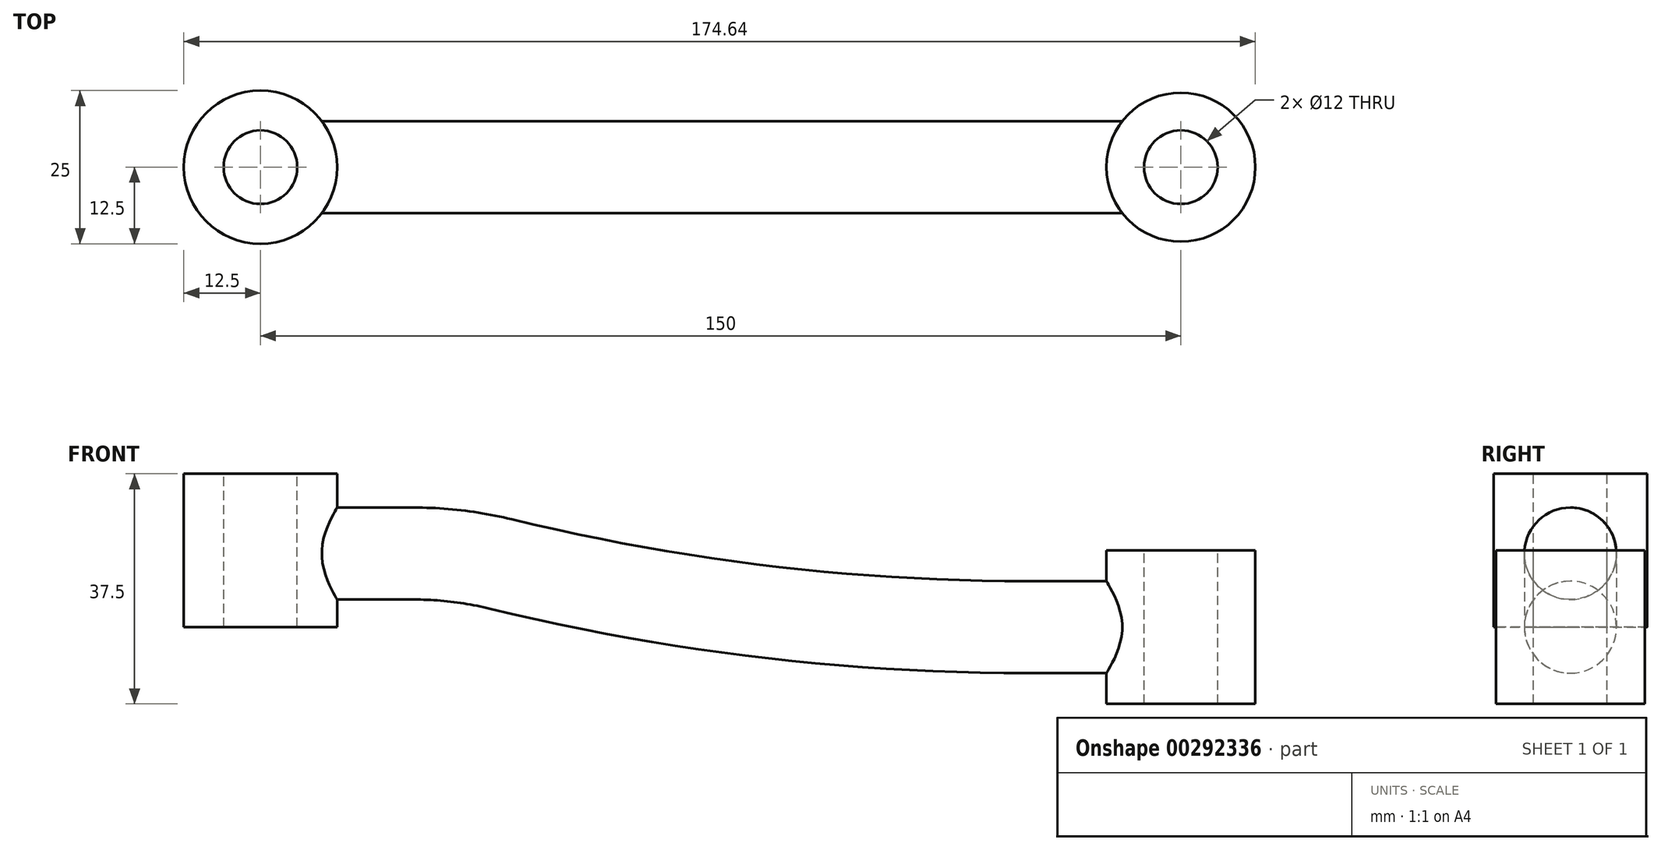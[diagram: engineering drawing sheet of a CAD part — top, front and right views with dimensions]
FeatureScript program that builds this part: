
annotation { "Feature Type Name" : "Feature", "Feature Type Description" : "" }
export const myFeature = defineFeature(function(context is Context, id is Id, definition is map)
    precondition{}
    {
        {
            var Q0;
            Q0=qCreatedBy(makeId("Top.planeOp"),FACE);
            var sketch = newSketch(context, id + "F0", { "sketchPlane" : qUnion([Q0])});
            skLineSegment(sketch, "E0", {"start": v(0, 0) * mm, "end": v(150, 0) * mm, "construction": true});
            skCircle(sketch, "E1", {"center": v(0, 0) * mm, "radius": 12.5 * mm});
            skCircle(sketch, "E2", {"center": v(150, 0) * mm, "radius": 12.14 * mm});
            skSolve(sketch);
        }
        {
            var Q0;
            Q0=makeQuery(id+"F0.imprint","IMPRINT",FACE,{"disambiguationData":[TD([[makeQuery(id+"F0.imprint","IMPRINT",EDGE,{"derivedFrom":sQuery(id+"F0.wireOp",EDGE,"E1")}),1.0]])]});
            extrude(context, id + "F1", {"entities" : qUnion([Q0]), "depth" : 25 * mm});
        }
        {
            var Q0;
            Q0=makeQuery(id+"F0.imprint","IMPRINT",FACE,{"disambiguationData":[TD([[makeQuery(id+"F0.imprint","IMPRINT",EDGE,{"derivedFrom":sQuery(id+"F0.wireOp",EDGE,"E2")}),1.0]])]});
            extrude(context, id + "F2", {"entities" : qUnion([Q0]), "endBound" : BoundingType.SYMMETRIC, "depth" : 25 * mm});
        }
        {
            var Q0;
            Q0=qCreatedBy(makeId("Front.planeOp"),FACE);
            var sketch = newSketch(context, id + "F3", { "sketchPlane" : qUnion([Q0])});
            skLineSegment(sketch, "E3", {"start": v(0, 12) * mm, "end": v(25, 12) * mm});
            skArc(sketch, "E4", {"start": v(25, 12) * mm, "mid": v(32.15, 11.57) * mm, "end": v(39.2, 10.3) * mm});
            skArc(sketch, "E5", {"start": v(39.2, 10.3) * mm, "mid": v(81.79, 2.58) * mm, "end": v(125, 0) * mm});
            skLineSegment(sketch, "E6", {"start": v(125, 0) * mm, "end": v(150, 0) * mm});
            skSolve(sketch);
        }
        {
            var Q0;
            Q0=qCreatedBy(makeId("Right.planeOp"),FACE);
            var sketch = newSketch(context, id + "F4", { "sketchPlane" : qUnion([Q0])});
            skCircle(sketch, "E7", {"center": v(0, 12) * mm, "radius": 7.5 * mm});
            skSolve(sketch);
        }
        {
            var Q0;
            Q0 = qSketchRegion(id + "F4", true);
            var Q1;
            Q1 = qConstructionFilter(qBodyType(qCreatedBy(id + "F3" ,EDGE), BodyType.WIRE), ConstructionObject.NO);
            sweep(context, id + "F5", {"operationType" : NewBodyOperationType.ADD, "profiles" : qUnion([Q0]), "path" : qUnion([Q1])});
        }
        {
            var Q0;
            Q0=qCreatedBy(makeId("Top.planeOp"),FACE);
            var sketch = newSketch(context, id + "F6", { "sketchPlane" : qUnion([Q0])});
            skCircle(sketch, "E8", {"center": v(0, 0) * mm, "radius": 6 * mm});
            skCircle(sketch, "E9", {"center": v(150, 0) * mm, "radius": 6 * mm});
            skSolve(sketch);
        }
        {
            var Q0;
            Q0 = qSketchRegion(id + "F6", true);
            extrude(context, id + "F7", {"entities" : qUnion([Q0]), "operationType" : NewBodyOperationType.REMOVE, "endBound" : BoundingType.THROUGH_ALL, "oppositeDirection" : true, "depth" : 25 * mm, "hasSecondDirection" : true, "secondDirectionBound" : SecondDirectionBoundingType.THROUGH_ALL, "secondDirectionOppositeDirection" : false, "secondDirectionDepth" : 25 * mm});
        }
    });
